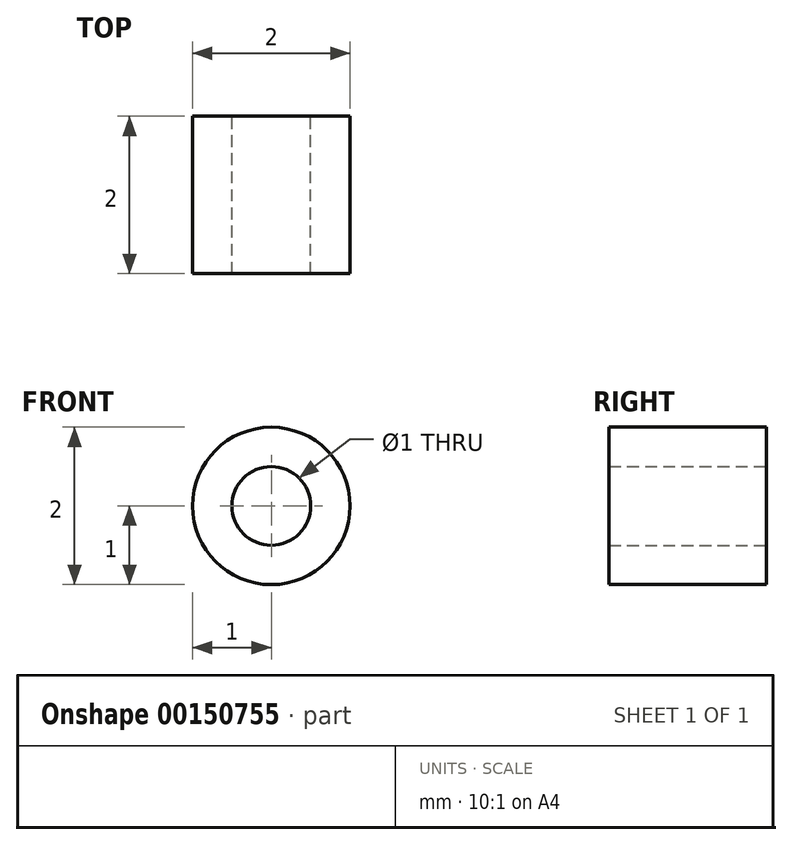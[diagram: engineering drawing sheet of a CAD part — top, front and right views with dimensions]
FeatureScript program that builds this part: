
annotation { "Feature Type Name" : "Feature", "Feature Type Description" : "" }
export const myFeature = defineFeature(function(context is Context, id is Id, definition is map)
    precondition{}
    {
        {
            var Q0;
            Q0=qCreatedBy(makeId("Front.planeOp"),FACE);
            var sketch = newSketch(context, id + "F0", { "sketchPlane" : qUnion([Q0])});
            skCircle(sketch, "E0", {"center": v(0, 0) * mm, "radius": 0.5 * mm});
            skCircle(sketch, "E1", {"center": v(0, 0) * mm, "radius": 1 * mm});
            skSolve(sketch);
        }
        {
            var Q0;
            Q0=makeQuery(id+"F0.imprint","IMPRINT",FACE,{"disambiguationData":[TD([[makeQuery(id+"F0.imprint","IMPRINT",EDGE,{"derivedFrom":sQuery(id+"F0.wireOp",EDGE,"E0")}),-1.0]])]});
            extrude(context, id + "F1", {"entities" : qUnion([Q0]), "depth" : 2 * mm});
        }
    });
